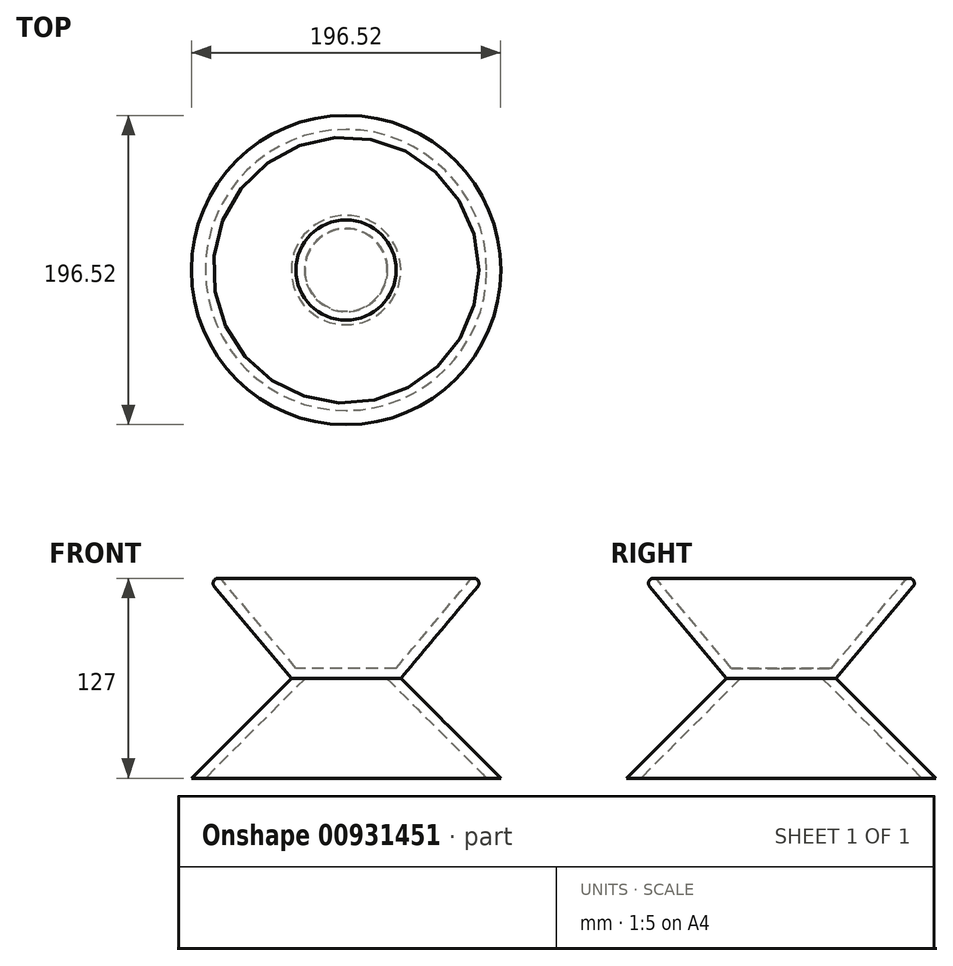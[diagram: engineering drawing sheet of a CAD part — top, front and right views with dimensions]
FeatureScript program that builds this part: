
annotation { "Feature Type Name" : "Feature", "Feature Type Description" : "" }
export const myFeature = defineFeature(function(context is Context, id is Id, definition is map)
    precondition{}
    {
        {
            var Q0;
            Q0=qCreatedBy(makeId("Top.planeOp"),FACE);
            var sketch = newSketch(context, id + "F0", { "sketchPlane" : qUnion([Q0])});
            skCircle(sketch, "E0", {"center": v(0, 0) * mm, "radius": 34.76 * mm});
            skSolve(sketch);
        }
        {
            var Q0;
            Q0 = qSketchRegion(id + "F0", true);
            extrude(context, id + "F1", {"entities" : qUnion([Q0]), "depth" : 63.5 * mm, "offsetDistance" : 25.4 * mm, "hasDraft" : true, "draftAngle" : 40 * degree});
        }
        {
            var Q0;
            Q0=makeQuery(id+"F1.opExtrude","CAP_FACE",FACE,{"disambiguationData":[OSD([sQuery(id+"F0.wireOp",EDGE,"E0")])],"isStart":false});
            shell(context, id + "F2", {"entities" : qUnion([Q0]), "thickness" : 6.35 * mm});
        }
        {
            var Q0;
            Q0=makeQuery(id+"F1.opExtrude","CAP_EDGE",EDGE,{"disambiguationData":[OSD([sQuery(id+"F0.wireOp",EDGE,"E0")])],"isStart":false});
            var Q1;
            {var subQ0=sQuery(id+"F0.wireOp",EDGE,"E0");Q1=makeQuery(id+"F2.opShell","OFFSET_EDGE",EDGE,{"disambiguationData":[OSD([subQ0]),TDD([makeQuery(id+"F1.opExtrude","CAP_EDGE",EDGE,{"disambiguationData":[OSD([subQ0])],"isStart":false})])]});}
            fillet(context, id + "F3", {"entities" : qUnion([Q0, Q1]), "radius" : 3.17 * mm, "tangentPropagation" : true, "allowEdgeOverflow" : false});
        }
        {
            var Q0;
            Q0=makeQuery(id+"F1.opExtrude","CAP_FACE",FACE,{"disambiguationData":[OSD([sQuery(id+"F0.wireOp",EDGE,"E0")])],"isStart":true});
            extrude(context, id + "F4", {"entities" : qUnion([Q0]), "operationType" : NewBodyOperationType.ADD, "depth" : 63.5 * mm, "offsetDistance" : 25.4 * mm, "hasDraft" : true, "draftAngle" : 45 * degree});
        }
        {
            var Q0;
            Q0=makeQuery(id+"F4.opExtrude","CAP_FACE",FACE,{"disambiguationData":[OSD([sQuery(id+"F0.wireOp",EDGE,"E0")])],"isStart":false});
            shell(context, id + "F5", {"entities" : qUnion([Q0]), "thickness" : 6.35 * mm});
        }
    });
